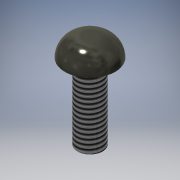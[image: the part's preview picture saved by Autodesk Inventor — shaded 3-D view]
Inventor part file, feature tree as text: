
AUTODESK INVENTOR PART (.ipt)
format: ipt  version: 2016 (Build 200138000, 138)  size: 143,872 bytes
history: native  units: mm
features: extrude x3, sketch x3, other x1, fillet x1, thread x1
ambient origin geometry x1: Origin
bodies: Body1 (feature_tree)
feature tree (9):
  other  "ソリッド1"
  extrude  "押し出し1"  Depth=4.0mm
  extrude  "押し出し2"  Depth=6.0mm TaperAngle=0.0deg
  fillet  "フィレット1"  Radius=8.0mm
  thread  "ねじ1"
  extrude  "押し出し3"  Depth=3.0mm TaperAngle=0.0deg
  sketch  "スケッチ1"
  sketch  "スケッチ2"
  sketch  "スケッチ3"
